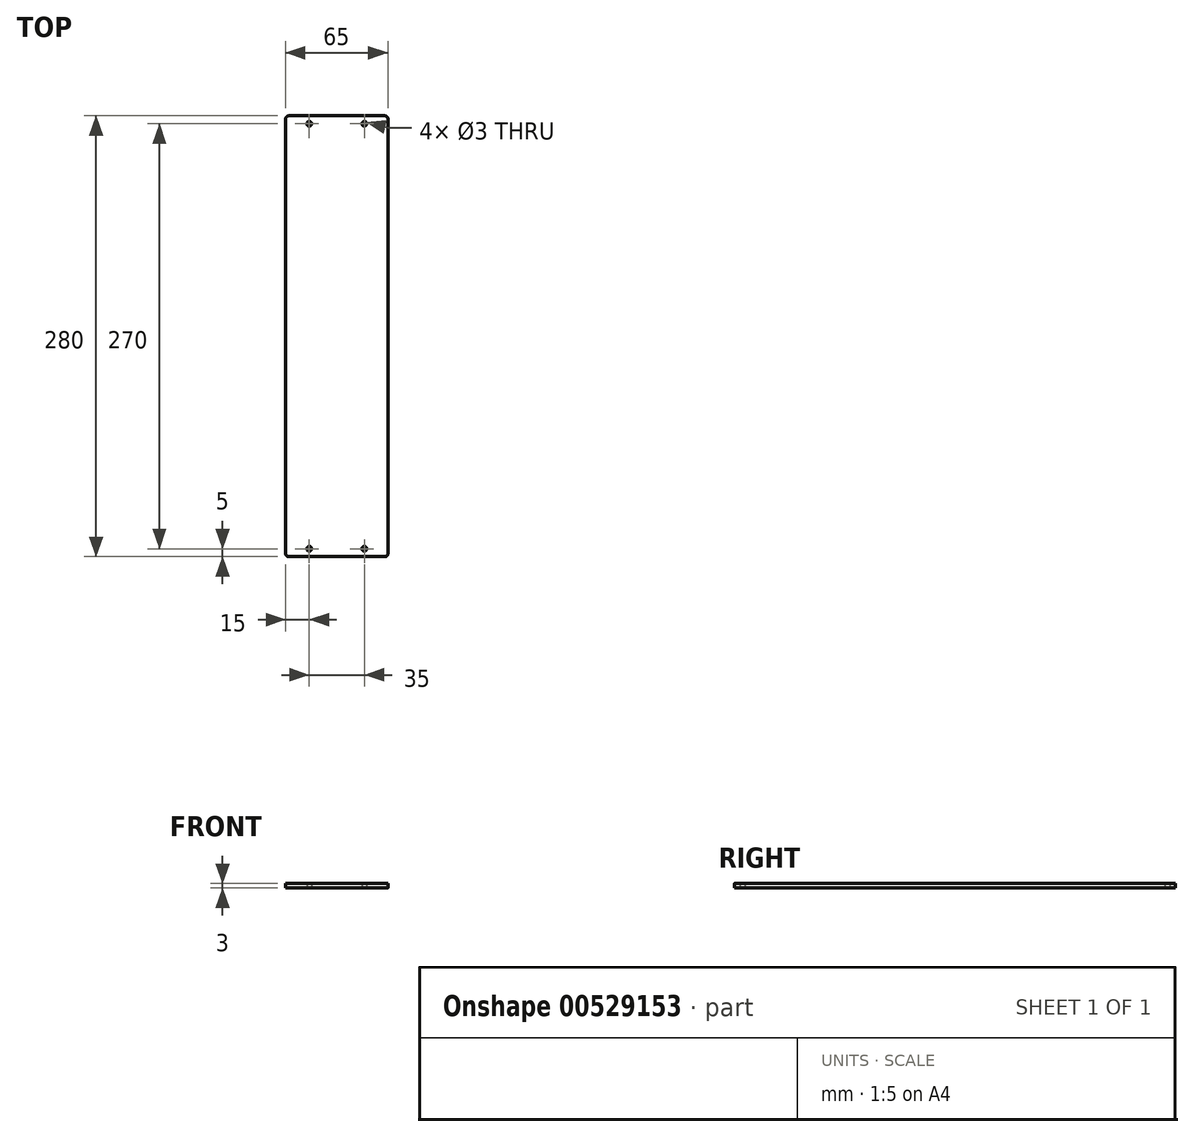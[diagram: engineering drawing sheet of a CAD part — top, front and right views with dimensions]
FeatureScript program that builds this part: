
annotation { "Feature Type Name" : "Feature", "Feature Type Description" : "" }
export const myFeature = defineFeature(function(context is Context, id is Id, definition is map)
    precondition{}
    {
        {
            var Q0;
            Q0=qCreatedBy(makeId("Top.planeOp"),FACE);
            var sketch = newSketch(context, id + "F0", { "sketchPlane" : qUnion([Q0])});
            skLineSegment(sketch, "E0.bottom", {"start": v(-30.5, 140) * mm, "end": v(30.5, 140) * mm});
            skLineSegment(sketch, "E0.top", {"start": v(-30.5, -140) * mm, "end": v(30.5, -140) * mm});
            skLineSegment(sketch, "E0.left", {"start": v(-32.5, 138) * mm, "end": v(-32.5, -138) * mm});
            skLineSegment(sketch, "E0.right", {"start": v(32.5, 138) * mm, "end": v(32.5, -138) * mm});
            skLineSegment(sketch, "E1", {"start": v(-17.5, 141.56) * mm, "end": v(-17.5, -144.63) * mm, "construction": true});
            skLineSegment(sketch, "E2", {"start": v(-37.83, 135) * mm, "end": v(37.33, 135) * mm, "construction": true});
            skLineSegment(sketch, "E3", {"start": v(0, 146.02) * mm, "end": v(0, -146.75) * mm, "construction": true});
            skPoint(sketch, "E3.startSnap0", {"position": v(0, 140) * mm});
            skPoint(sketch, "E3.endSnap0", {"position": v(0, -140) * mm});
            skLineSegment(sketch, "E4.MirrorCS", {"start": v(17.5, 141.56) * mm, "end": v(17.5, -144.63) * mm, "construction": true});
            skLineSegment(sketch, "E5", {"start": v(-42.31, 0) * mm, "end": v(45.96, 0) * mm, "construction": true});
            skPoint(sketch, "E5.startSnap0", {"position": v(-32.5, 0) * mm});
            skPoint(sketch, "E5.endSnap0", {"position": v(32.5, 0) * mm});
            skLineSegment(sketch, "E6.MirrorCS", {"start": v(-37.83, -135) * mm, "end": v(37.33, -135) * mm, "construction": true});
            skCircle(sketch, "E7", {"center": v(-17.5, 135) * mm, "radius": 1.5 * mm});
            skCircle(sketch, "E8.MirrorC", {"center": v(17.5, 135) * mm, "radius": 1.5 * mm});
            skCircle(sketch, "E9.MirrorC", {"center": v(-17.5, -135) * mm, "radius": 1.5 * mm});
            skCircle(sketch, "E10.MirrorC", {"center": v(17.5, -135) * mm, "radius": 1.5 * mm});
            skPoint(sketch, "E11.visualSharp", {"position": v(-32.5, 140) * mm});
            skArc(sketch, "E11.filletArc", {"start": v(-30.5, 140) * mm, "mid": v(-31.91, 139.41) * mm, "end": v(-32.5, 138) * mm});
            skPoint(sketch, "E12.visualSharp", {"position": v(32.5, 140) * mm});
            skArc(sketch, "E12.filletArc", {"start": v(32.5, 138) * mm, "mid": v(31.91, 139.41) * mm, "end": v(30.5, 140) * mm});
            skPoint(sketch, "E13.visualSharp", {"position": v(-32.5, -140) * mm});
            skArc(sketch, "E13.filletArc", {"start": v(-32.5, -138) * mm, "mid": v(-31.91, -139.41) * mm, "end": v(-30.5, -140) * mm});
            skPoint(sketch, "E14.visualSharp", {"position": v(32.5, -140) * mm});
            skArc(sketch, "E14.filletArc", {"start": v(30.5, -140) * mm, "mid": v(31.91, -139.41) * mm, "end": v(32.5, -138) * mm});
            skSolve(sketch);
        }
        {
            var Q0;
            Q0=makeQuery(id+"F0.imprint","IMPRINT",FACE,{"disambiguationData":[TD([[makeQuery(id+"F0.imprint","IMPRINT",EDGE,{"derivedFrom":sQuery(id+"F0.wireOp",EDGE,"E0.bottom")}),-1.0]])]});
            extrude(context, id + "F1", {"entities" : qUnion([Q0]), "depth" : 3 * mm, "offsetDistance" : 25 * mm});
        }
    });
